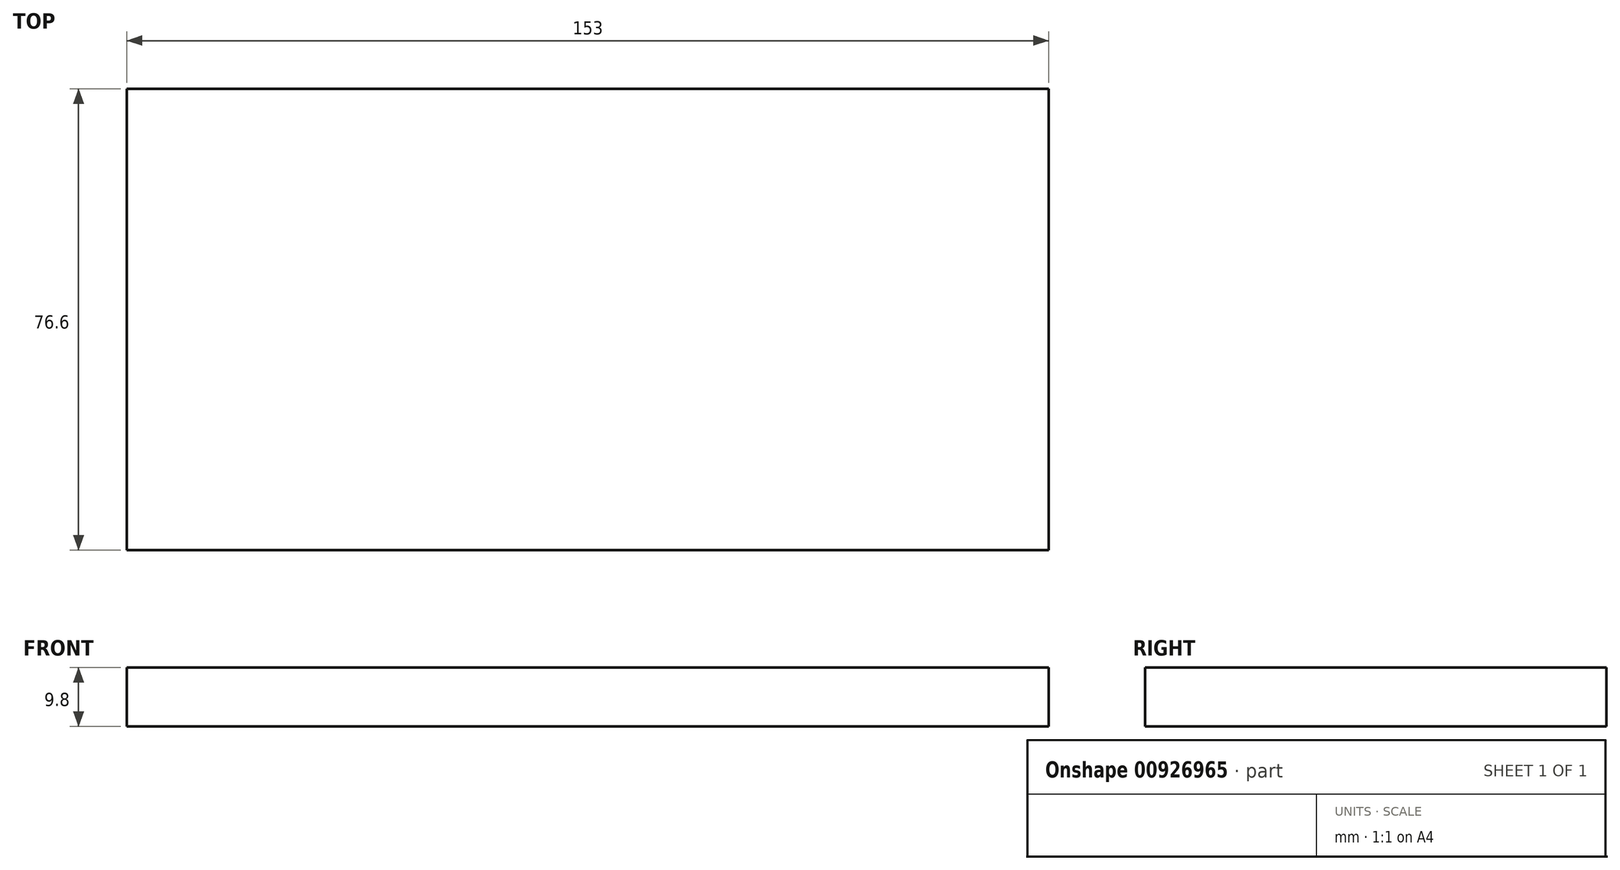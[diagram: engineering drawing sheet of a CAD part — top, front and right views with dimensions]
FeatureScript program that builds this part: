
annotation { "Feature Type Name" : "Feature", "Feature Type Description" : "" }
export const myFeature = defineFeature(function(context is Context, id is Id, definition is map)
    precondition{}
    {
        {
            var Q0;
            Q0=qCreatedBy(makeId("Top.planeOp"),FACE);
            var sketch = newSketch(context, id + "F0", { "sketchPlane" : qUnion([Q0])});
            skLineSegment(sketch, "E0.bottom", {"start": v(76.5, 38.3) * mm, "end": v(-76.5, 38.3) * mm});
            skLineSegment(sketch, "E0.top", {"start": v(76.5, -38.3) * mm, "end": v(-76.5, -38.3) * mm});
            skLineSegment(sketch, "E0.left", {"start": v(76.5, 38.3) * mm, "end": v(76.5, -38.3) * mm});
            skLineSegment(sketch, "E0.right", {"start": v(-76.5, 38.3) * mm, "end": v(-76.5, -38.3) * mm});
            skPoint(sketch, "E0.middle", {"position": v(0, 0) * mm});
            skSolve(sketch);
        }
        {
            var Q0;
            Q0 = qSketchRegion(id + "F0", true);
            extrude(context, id + "F1", {"entities" : qUnion([Q0]), "depth" : 9.8 * mm, "offsetDistance" : 25 * mm});
        }
    });
